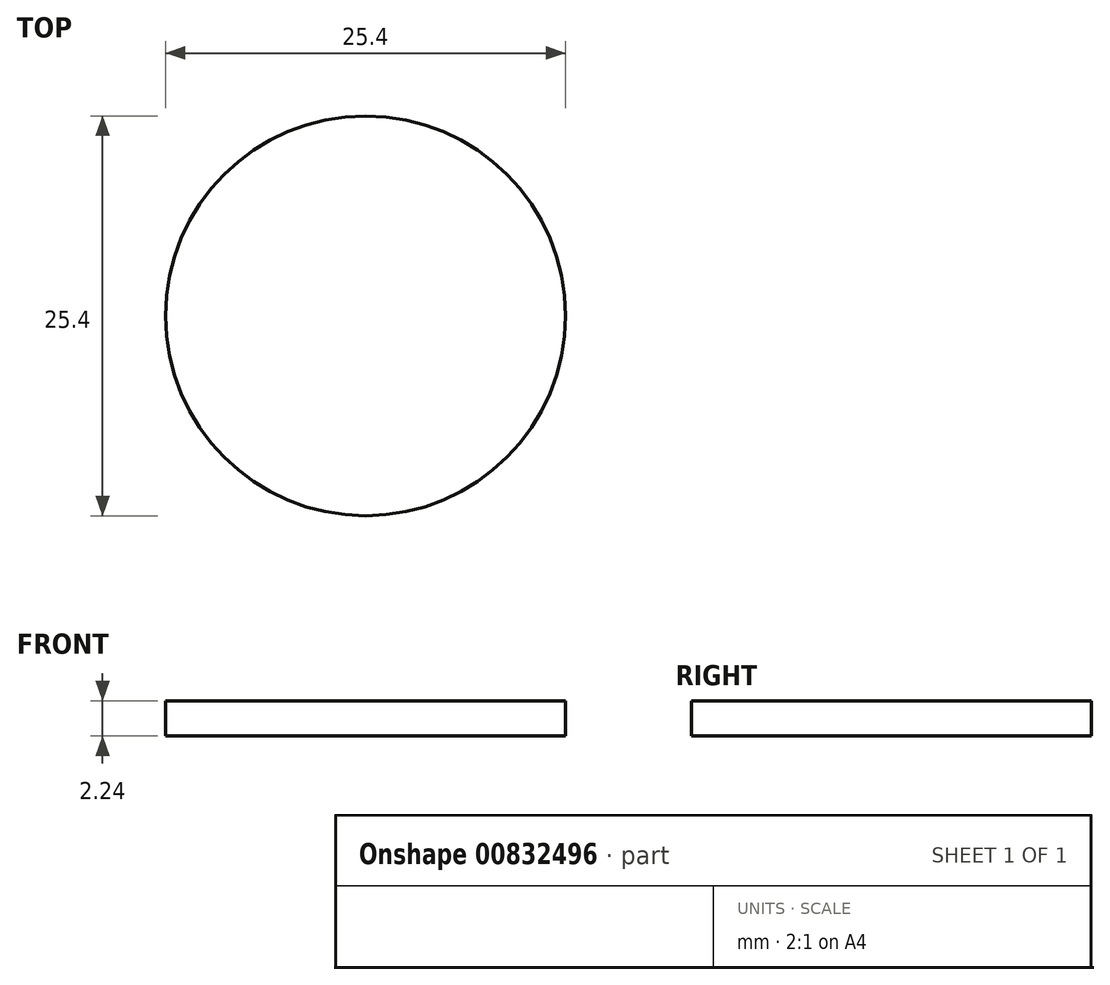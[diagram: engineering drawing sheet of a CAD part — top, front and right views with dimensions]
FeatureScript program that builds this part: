
annotation { "Feature Type Name" : "Feature", "Feature Type Description" : "" }
export const myFeature = defineFeature(function(context is Context, id is Id, definition is map)
    precondition{}
    {
        {
            var Q0;
            Q0=qCreatedBy(makeId("Top.planeOp"),FACE);
            var sketch = newSketch(context, id + "F0", { "sketchPlane" : qUnion([Q0])});
            skCircle(sketch, "E0", {"center": v(0, 0) * mm, "radius": 12.7 * mm});
            skSolve(sketch);
        }
        {
            var Q0;
            Q0 = qSketchRegion(id + "F0", true);
            extrude(context, id + "F1", {"entities" : qUnion([Q0]), "depth" : 2.24 * mm, "offsetDistance" : 25.4 * mm});
        }
    });
